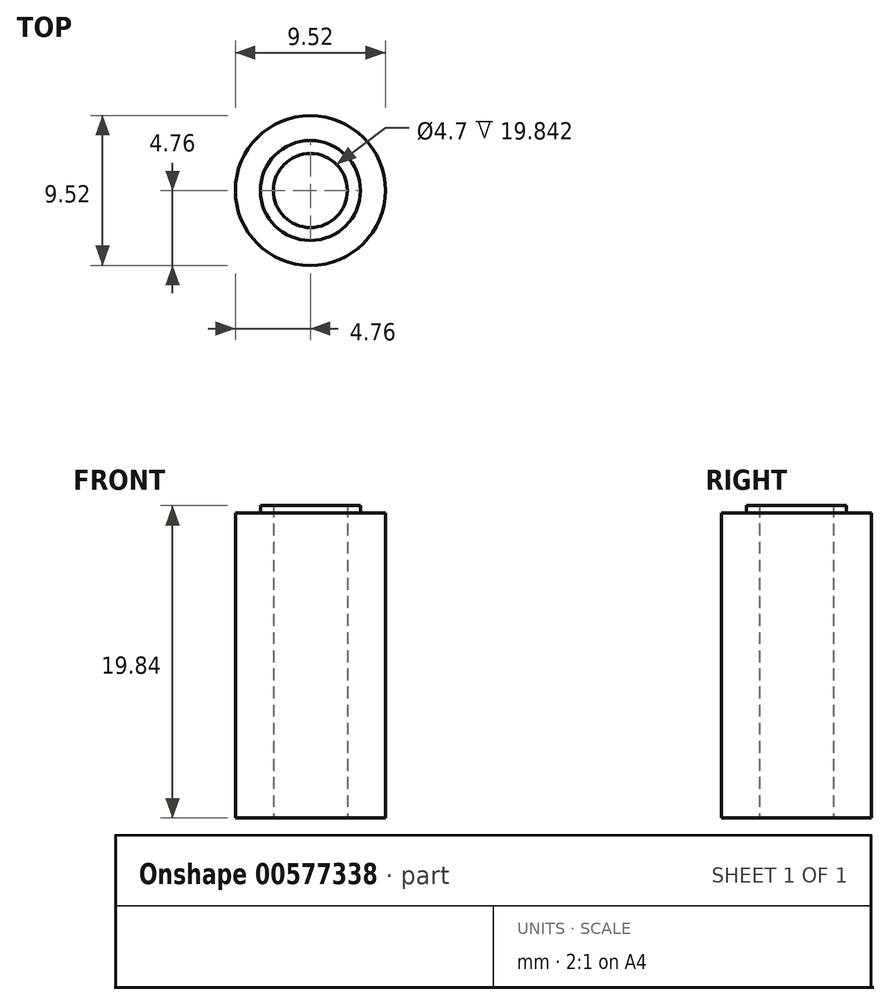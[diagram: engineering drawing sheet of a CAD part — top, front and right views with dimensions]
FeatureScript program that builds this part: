
annotation { "Feature Type Name" : "Feature", "Feature Type Description" : "" }
export const myFeature = defineFeature(function(context is Context, id is Id, definition is map)
    precondition{}
    {
        {
            var Q0;
            Q0=qCreatedBy(makeId("Top.planeOp"),FACE);
            var sketch = newSketch(context, id + "F0", { "sketchPlane" : qUnion([Q0])});
            skCircle(sketch, "E0", {"center": v(0, 0) * mm, "radius": 2.35 * mm});
            skCircle(sketch, "E1", {"center": v(0, 0) * mm, "radius": 4.76 * mm});
            skSolve(sketch);
        }
        {
            var Q0;
            Q0 = qSketchRegion(id + "F0", true);
            extrude(context, id + "F1", {"entities" : qUnion([Q0]), "endBound" : BoundingType.SYMMETRIC, "depth" : 19.84 * mm, "offsetDistance" : 25.4 * mm});
        }
        {
            var Q0;
            Q0=makeQuery(id+"F1.opExtrude","CAP_FACE",FACE,{"disambiguationData":[OSD([sQuery(id+"F0.wireOp",EDGE,"E0"),sQuery(id+"F0.wireOp",EDGE,"E1")])],"isStart":false});
            var sketch = newSketch(context, id + "F2", { "sketchPlane" : qUnion([Q0])});
            skCircle(sketch, "E2", {"center": v(0, 0) * mm, "radius": 3.18 * mm});
            skCircle(sketch, "E3", {"center": v(0, 0) * mm, "radius": 2.35 * mm});
            skCircle(sketch, "E4", {"center": v(0, 0) * mm, "radius": 4.76 * mm});
            skSolve(sketch);
        }
        {
            var Q0;
            Q0=makeQuery(id+"F2.imprint","IMPRINT",FACE,{"disambiguationData":[TD([[makeQuery(id+"F2.imprint","IMPRINT",EDGE,{"derivedFrom":sQuery(id+"F2.wireOp",EDGE,"E2")}),-1.0]])]});
            extrude(context, id + "F3", {"entities" : qUnion([Q0]), "operationType" : NewBodyOperationType.REMOVE, "oppositeDirection" : true, "depth" : 0.48 * mm, "offsetDistance" : 25.4 * mm});
        }
    });
